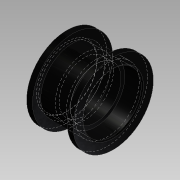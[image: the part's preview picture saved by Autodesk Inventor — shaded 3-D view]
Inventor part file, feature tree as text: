
AUTODESK INVENTOR PART (.ipt)
format: ipt  version: 2013 SP2 (Build 170200200, 200)  size: 126,976 bytes
history: native  units: mm
features: revolve x1, sketch x1
ambient origin geometry x8: Origin, YZ Plane, XZ Plane, XY Plane, X Axis, Y Axis, Z Axis, Center Point
bodies: Solid1 (feature_tree)
feature tree (2):
  revolve  "Revolution1"  [1 undecoded]
  sketch  "Sketch1"  dims[d0=5.0mm d1=1.55mm d2=13.89mm d3=15.974mm d5=22.0mm d6=17.5mm d7=1.6mm d8=4.75mm d9=0.3mm d10=0.3mm d11=90.0deg]
note: 1 required parameter value undecoded (feature->parameter linkage not recoverable at this tier; creation-order binding heuristic only, values carry confidence <= 0.55)
